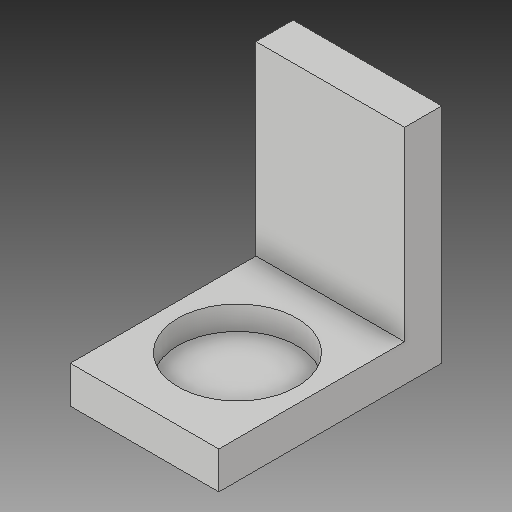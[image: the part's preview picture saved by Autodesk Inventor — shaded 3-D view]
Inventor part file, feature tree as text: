
AUTODESK INVENTOR PART (.ipt)
format: ipt  version: 2019 (Build 230136000, 136)  size: 122,368 bytes
history: native  units: in
note: dims shown in document units (in); Inventor stores cm internally (conversion verified against a paired STEP export)
features: sketch x2, other x1, extrude x1, hole x1, projected_geometry x1
ambient origin geometry x8: Origin, YZ Plane, XZ Plane, XY Plane, X Axis, Y Axis, Z Axis, Center Point
bodies: Solid1 (feature_tree)
feature tree (6):
  other  "spring tab for on arm"
  extrude  "Extrusion1"  Depth=0.75in
  hole  "Hole2"  [1 undecoded]
  sketch  "Sketch1"  dims[d0=0.125in d1=0.75in]
  sketch  "Sketch3"  dims[d4=0.125in d5=0.75in d6=0.5in d7=0.0in d15=0.4in d16=0.75in d17=0.375in d18=0.25in d19=0.5635in d20=0.08in d21=0.0in]
  projected_geometry  "Projected Loop2"
note: 1 required parameter value undecoded (feature->parameter linkage not recoverable at this tier; creation-order binding heuristic only, values carry confidence <= 0.55)
